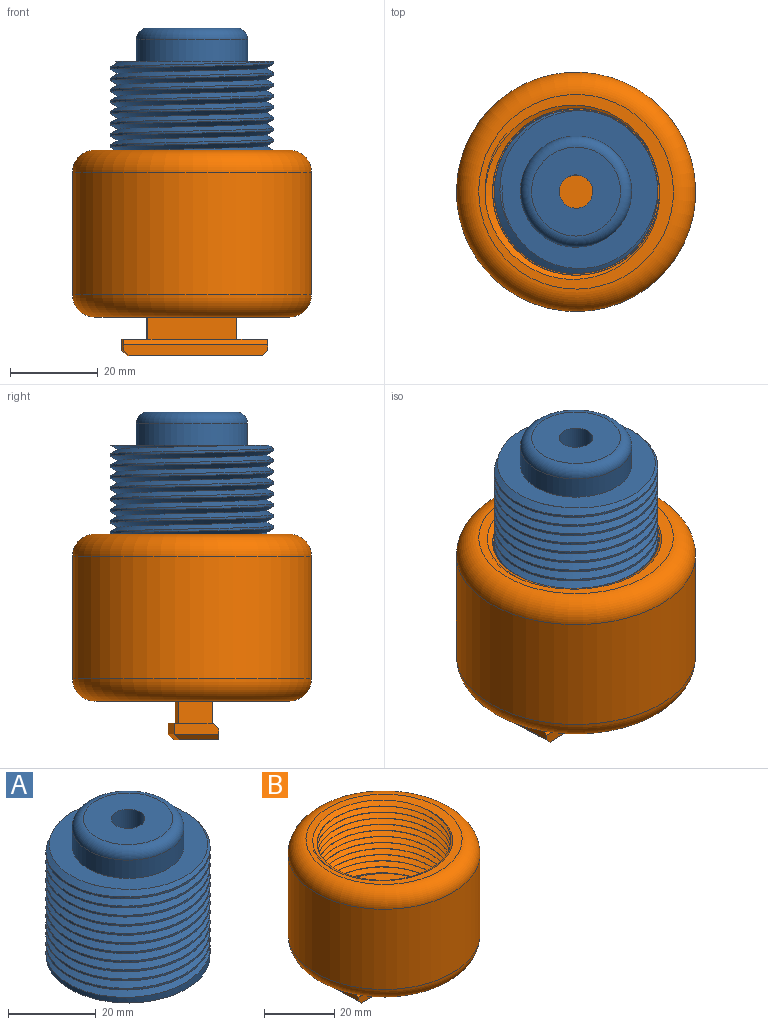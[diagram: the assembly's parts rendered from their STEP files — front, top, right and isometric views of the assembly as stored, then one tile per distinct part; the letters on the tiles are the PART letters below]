
ASSEMBLY  parts=2 mates=1
PART A: 10 faces, bbox 38.5x44.3x39.3 mm
  f0: cylinder r=18.67mm len=37.34mm, axis (0,0,-1), area 1118.7mm2, adj f1,f2,f7,f8,f9
  f1: plane 37.26x37.24mm, normal (0,0,1), area 508.4mm2, adj f0,f3,f8,f9
  f2: plane 37.34x37.34mm, normal (0,0,-1), area 1049.3mm2, adj f0,f5
  f3: cylinder r=12.7mm len=25.4mm, axis (0,0,-1), area 405.4mm2, adj f1,f6
  f4: plane 20.32x20.32mm, normal (0,0,1), area 278.7mm2, adj f5,f6
  f5: cylinder r=3.81mm len=38.1mm, axis (0,0,1), area 912.1mm2, adj f2,f4
  f6: torus R=10.16mm, axis (0,0,1), area 295.2mm2, adj f3,f4
  f7: plane 2.03x1.76mm, normal (0,1,0.02), area 1.8mm2, adj f0,f8,f9
  f8: bspline ~43.11x37.34mm, area 2687.8mm2, adj f0,f1,f7,f9
  f9: bspline ~37.34x37.27mm, area 2591.4mm2, adj f0,f1,f7,f8
PART B: 24 faces, bbox 60.6x60.6x49.8 mm
  f0: cylinder r=19.05mm len=38.1mm, axis (0,0,1), area -135.5mm2, adj f2,f4,f21,f22,f23
  f1: cylinder r=27.3mm len=54.61mm, axis (0,0,-1), area 4793.5mm2, adj f5,f6
  f2: plane 45.98x45.98mm, normal (0,0,1), area 307.5mm2, adj f0,f6,f22,f23
  f3: plane 44.45x44.45mm, normal (0,0,-1), area 1397mm2, adj f5,f7,f8,f9,f10
  f4: plane 38.1x38.1mm, normal (0,0,1), area 1140.1mm2, adj f0
  f5: torus R=22.23mm, axis (0,0,1), area 1276.5mm2, adj f1,f3
  f6: torus R=22.23mm, axis (0,0,1), area 1276.5mm2, adj f1,f2
  f7: plane 7.62x5.12mm, normal (-1,0,0), area 38.7mm2, adj f3,f8,f10,f16,f20
  f8: plane 20.32x5.08mm, normal (0,1,0), area 103.2mm2, adj f3,f7,f9,f16
  f9: plane 7.62x5.12mm, normal (1,0,0), area 38.7mm2, adj f3,f8,f10,f16,f20
  f10: plane 20.32x5.12mm, normal (0,-1,0), area 104.1mm2, adj f3,f7,f9,f20
  f11: plane 10.16x2.54mm, normal (-1,0,0), area 25mm2, adj f12,f14,f16,f19,f20
  f12: plane 33.02x2.54mm, normal (0,1,0), area 83.9mm2, adj f11,f13,f16,f18
  f13: plane 10.16x2.54mm, normal (1,0,0), area 25mm2, adj f12,f14,f16,f17,f20
  f14: plane 33.02x2.54mm, normal (0,-1,0), area 82.3mm2, adj f11,f13,f15,f17,f19,f20
  f15: plane 30.48x8.89mm, normal (0,0,-1), area 271mm2, adj f14,f17,f18,f19
  f16: plane 33.02x8.89mm, normal (0,0,1), area 139.5mm2, adj f7,f8,f9,f11,f12,f13,f20
  f17: plane 10.16x1.27mm, normal (0.71,0,-0.71), area 17.1mm2, adj f13,f14,f15,f18
  f18: plane 33.02x1.27mm, normal (0,0.71,-0.71), area 57mm2, adj f12,f15,f17,f19
  f19: plane 10.16x1.27mm, normal (-0.71,0,-0.71), area 17.1mm2, adj f11,f14,f15,f18
  f20: plane 33.02x1.27mm, normal (0,-0.71,0.71), area 58.1mm2, adj f7,f9,f10,f11,f13,f14,f16
  f21: plane 2.03x1.76mm, normal (0,1,0.02), area 1.8mm2, adj f0,f22,f23
  f22: bspline ~48.06x41.64mm, area 2985.2mm2, adj f0,f2,f21,f23
  f23: bspline ~48.06x41.64mm, area 2835.9mm2, adj f0,f2,f21,f22
PLACE A rot(axis=(0,0,1),2.4deg) t=(-3.81,-57.66,-31.45)mm
PLACE B rot(axis=(0,0,1),2.4deg) t=(-3.81,-57.66,-59.34)mm
MATE cylindrical A.f0 <-> B.f0  axis (0,0,-1) through (-3.81,-57.66,-31.45)mm
